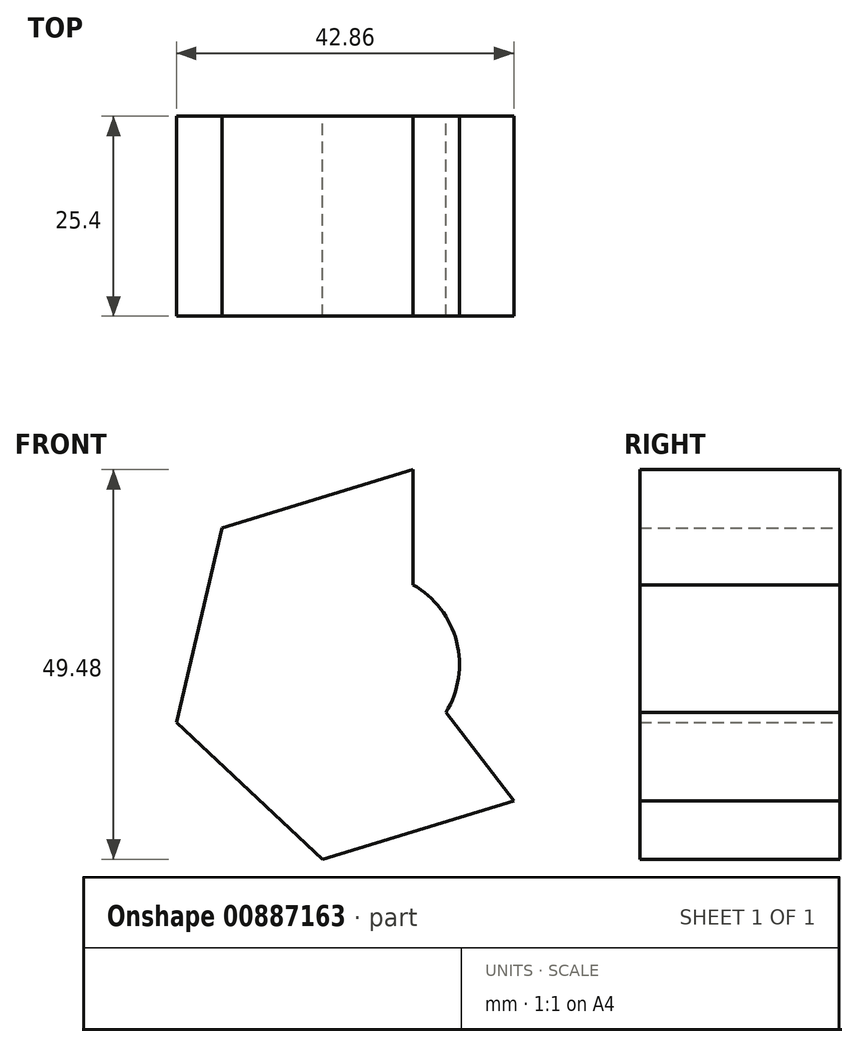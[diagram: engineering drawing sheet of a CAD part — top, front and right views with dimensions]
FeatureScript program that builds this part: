
annotation { "Feature Type Name" : "Feature", "Feature Type Description" : "" }
export const myFeature = defineFeature(function(context is Context, id is Id, definition is map)
    precondition{}
    {
        {
            var Q0;
            Q0=qCreatedBy(makeId("Front.planeOp"),FACE);
            var sketch = newSketch(context, id + "F0", { "sketchPlane" : qUnion([Q0])});
            skLineSegment(sketch, "E0.0", {"start": v(-18.55, 17.36) * mm, "end": v(5.76, 24.74) * mm});
            skLineSegment(sketch, "E0.1", {"start": v(5.76, 24.74) * mm, "end": v(5.76, -0.66) * mm});
            skLineSegment(sketch, "E0.2", {"start": v(5.76, -0.66) * mm, "end": v(18.55, -17.36) * mm});
            skLineSegment(sketch, "E0.3", {"start": v(18.55, -17.36) * mm, "end": v(-5.76, -24.74) * mm});
            skLineSegment(sketch, "E0.4", {"start": v(-5.76, -24.74) * mm, "end": v(-24.3, -7.39) * mm});
            skLineSegment(sketch, "E0.5", {"start": v(-24.3, -7.39) * mm, "end": v(-18.55, 17.36) * mm});
            skPoint(sketch, "E0.0.midPoint", {"position": v(-6.4, 21.05) * mm});
            skCircle(sketch, "E1", {"center": v(0, 0) * mm, "radius": 11.64 * mm});
            skSolve(sketch);
        }
        {
            var Q0;
            Q0 = qSketchRegion(id + "F0", true);
            extrude(context, id + "F1", {"entities" : qUnion([Q0]), "depth" : 25.4 * mm, "offsetDistance" : 25.4 * mm});
        }
    });
